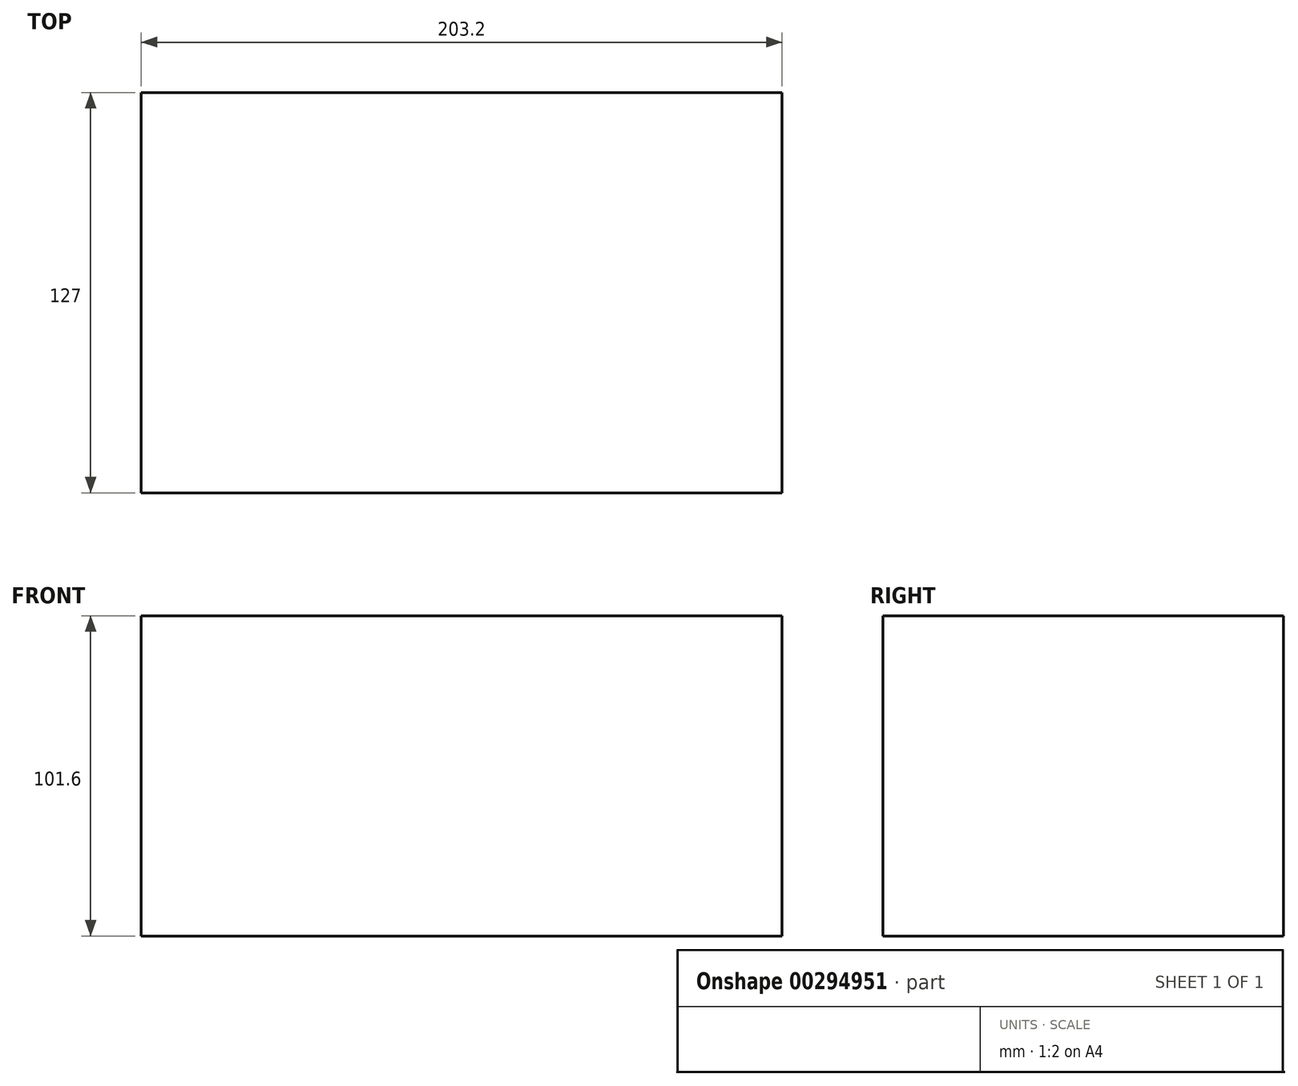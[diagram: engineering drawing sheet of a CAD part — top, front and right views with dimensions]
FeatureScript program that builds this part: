
annotation { "Feature Type Name" : "Feature", "Feature Type Description" : "" }
export const myFeature = defineFeature(function(context is Context, id is Id, definition is map)
    precondition{}
    {
        {
            var Q0;
            Q0=qCreatedBy(makeId("Top.planeOp"),FACE);
            var sketch = newSketch(context, id + "F0", { "sketchPlane" : qUnion([Q0])});
            skLineSegment(sketch, "E0.bottom", {"start": v(-93.33, 70.01) * mm, "end": v(109.87, 70.01) * mm});
            skLineSegment(sketch, "E0.top", {"start": v(-93.33, -56.99) * mm, "end": v(109.87, -56.99) * mm});
            skLineSegment(sketch, "E0.left", {"start": v(-93.33, 70.01) * mm, "end": v(-93.33, -56.99) * mm});
            skLineSegment(sketch, "E0.right", {"start": v(109.87, 70.01) * mm, "end": v(109.87, -56.99) * mm});
            skSolve(sketch);
        }
        {
            var Q0;
            Q0=makeQuery(id+"F0.imprint","IMPRINT",FACE,{"disambiguationData":[TD([[makeQuery(id+"F0.imprint","IMPRINT",EDGE,{"derivedFrom":sQuery(id+"F0.wireOp",EDGE,"E0.bottom")}),-1.0]])]});
            extrude(context, id + "F1", {"entities" : qUnion([Q0]), "depth" : 101.6 * mm});
        }
    });
